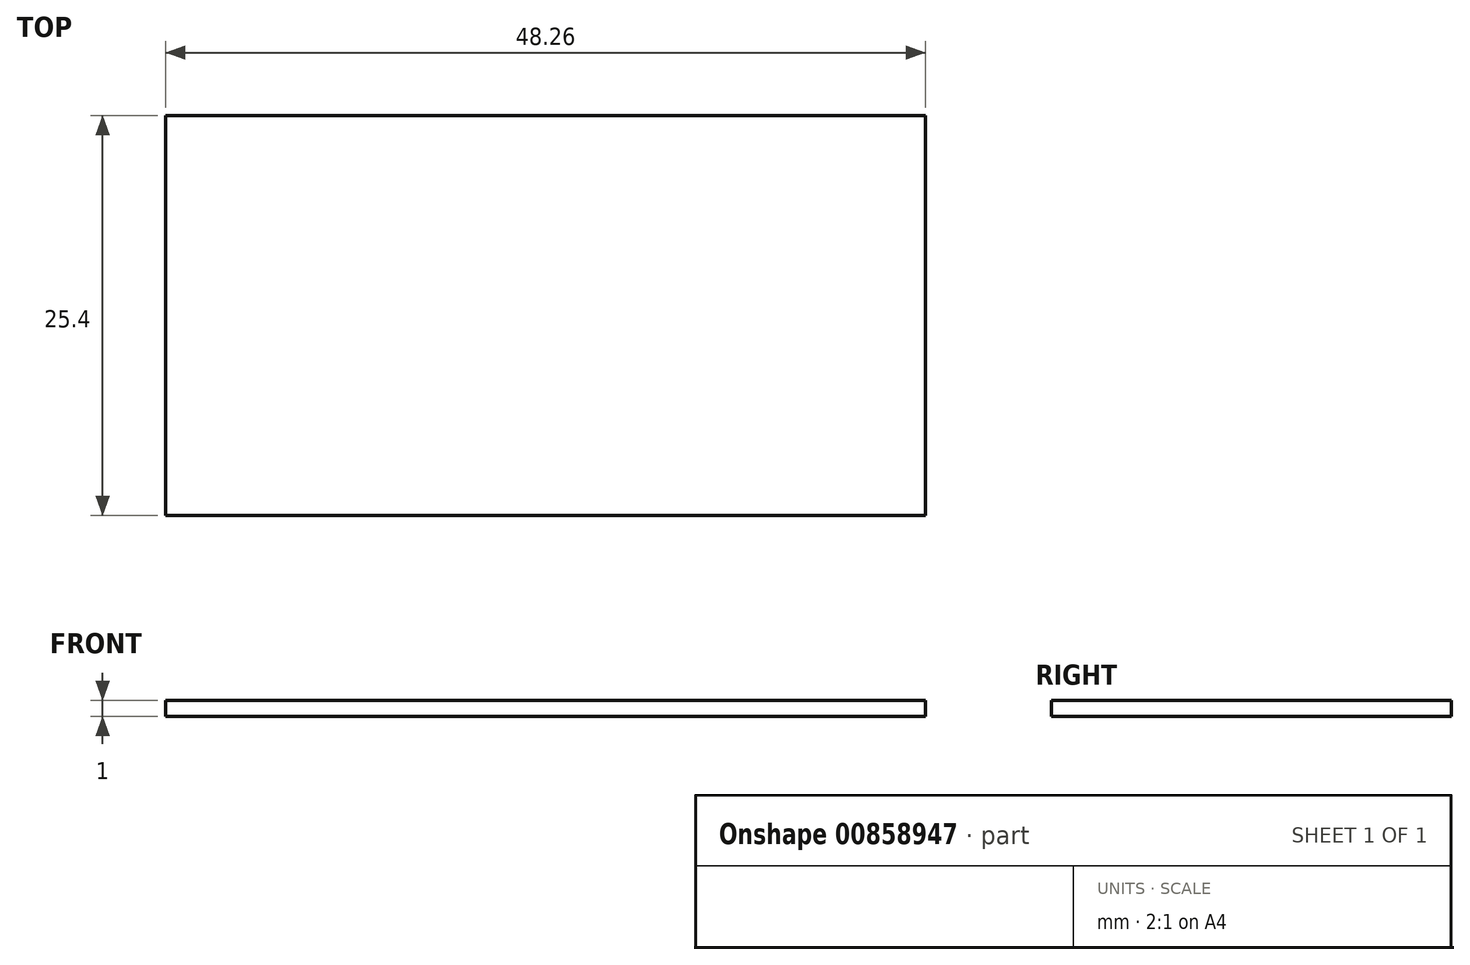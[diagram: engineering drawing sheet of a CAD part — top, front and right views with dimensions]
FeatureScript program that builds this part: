
annotation { "Feature Type Name" : "Feature", "Feature Type Description" : "" }
export const myFeature = defineFeature(function(context is Context, id is Id, definition is map)
    precondition{}
    {
        {
            var Q0;
            Q0=qCreatedBy(makeId("Top.planeOp"),FACE);
            var sketch = newSketch(context, id + "F0", { "sketchPlane" : qUnion([Q0])});
            skLineSegment(sketch, "E0.bottom", {"start": v(24.13, 12.7) * mm, "end": v(-24.13, 12.7) * mm});
            skLineSegment(sketch, "E0.top", {"start": v(24.13, -12.7) * mm, "end": v(-24.13, -12.7) * mm});
            skLineSegment(sketch, "E0.left", {"start": v(24.13, 12.7) * mm, "end": v(24.13, -12.7) * mm});
            skLineSegment(sketch, "E0.right", {"start": v(-24.13, 12.7) * mm, "end": v(-24.13, -12.7) * mm});
            skPoint(sketch, "E0.middle", {"position": v(0, 0) * mm});
            skSolve(sketch);
        }
        {
            var Q0;
            Q0 = qSketchRegion(id + "F0", true);
            extrude(context, id + "F1", {"entities" : qUnion([Q0]), "depth" : 1 * mm, "offsetDistance" : 25.4 * mm});
        }
    });
